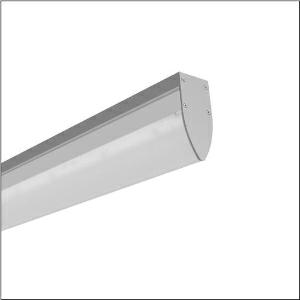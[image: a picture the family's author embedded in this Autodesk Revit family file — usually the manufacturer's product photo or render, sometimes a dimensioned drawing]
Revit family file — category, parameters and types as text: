
# Revit family: mira_r__21_td_51fr527g434a_c56a
name_source: partatom
category: Lighting Fixtures
units: mm (PartAtom-declared; Revit-internal decimal feet)

## family parameters
Cut with Voids When Loaded = No
Host = Face
Light Source = No
Part Type = Normal
Room Calculation Point = No
Round Connector Dimension = Use Diameter
Shared = No

## types (1)
- Mira® 21 TD (1 x LED, 3020 lm, 20 W, 4000K)
    Apparent Load = 20 VA
    CIE Flux Codes = 40 68 87 81 100
    Color Rendering = 80
    Color Temperature = 4000K
    Default Elevation = 1800 mm
    Description = Mira® 21 TD, clean room luminaire, primary light control with reflector, primary optical cover: cover, of PMMA, frosted, light emission: direct distribution, primary light characteristic: symmetric, installation type: surface-mounted, LED, rated luminous flux: 3.020lm, luminous efficacy: 151lm/W, light colour: 840, colour temperature: 4000K, control gear: ECG, with terminal, 3-pole, max. 2.5mm², mains connection: 230V, AC, 50/60Hz, rated input power: 20W, luminaire housing, of sheet steel, coated, pure white (RAL 9010), length: 900mm, width: 55mm, height: 120mm, protection rating (complete): IP43, insulation class (complete): insulation class I (protective earthing), certification: CE, UKCA, permissible operating ambient temperature: -5..+40°C, standard: EN 50419, packaging unit: 1 piece
    Height = 0 mm  [stored 0 ft]
    Lamp = 1 x LED
    Lamp Light Flux = 3020 lm
    Lamp Power = 20 W
    Lamp count = 1
    Length = 900 mm
    Luminous efficacy = 151 lm/W
    Manufacturer = Siteco
    ModVariant = No
    Model = 51FR527G434A
    Mounting Place = Ceiling
    Mounting Type = Recessed
    Number of Poles = 1
    OnlyDefault = Yes
    Power Factor = 1
    Product Name = Mira® 21 TD
    Product group = clean room luminaire
    ProductGroupID = 402
    Protection Class = Protection class I
    Protection Degree = IP 43
    RLX_Detail_Level = 1
    RLX_Emergency_Light_Flux = 0 lm
    RLX_Emergency_Type = 0
    RLX_Emergency_Type_DB = No
    RlxData = <blob elided: 25109 chars, md5=ed6e0eb2>
    Socket = socket
    Standby Power = 0 W
    System Light Flux = 3020 lm
    System Power = 20 W
    Type Comments = Product without accessories
    Type Image = l_1007115.jpg
    URL = http://relux.com
    VarID = ---
    Voltage = 0 V
    Weight = 0.00 kg
    Width = 55 mm

note: [stored X ft] marks values corroborated as IEEE doubles in the binary element streams (Revit-internal decimal feet)

## geometry (parser evidence)
native form markers: Blend x4, Sweep x13
no freeform markers — native parametric forms only
